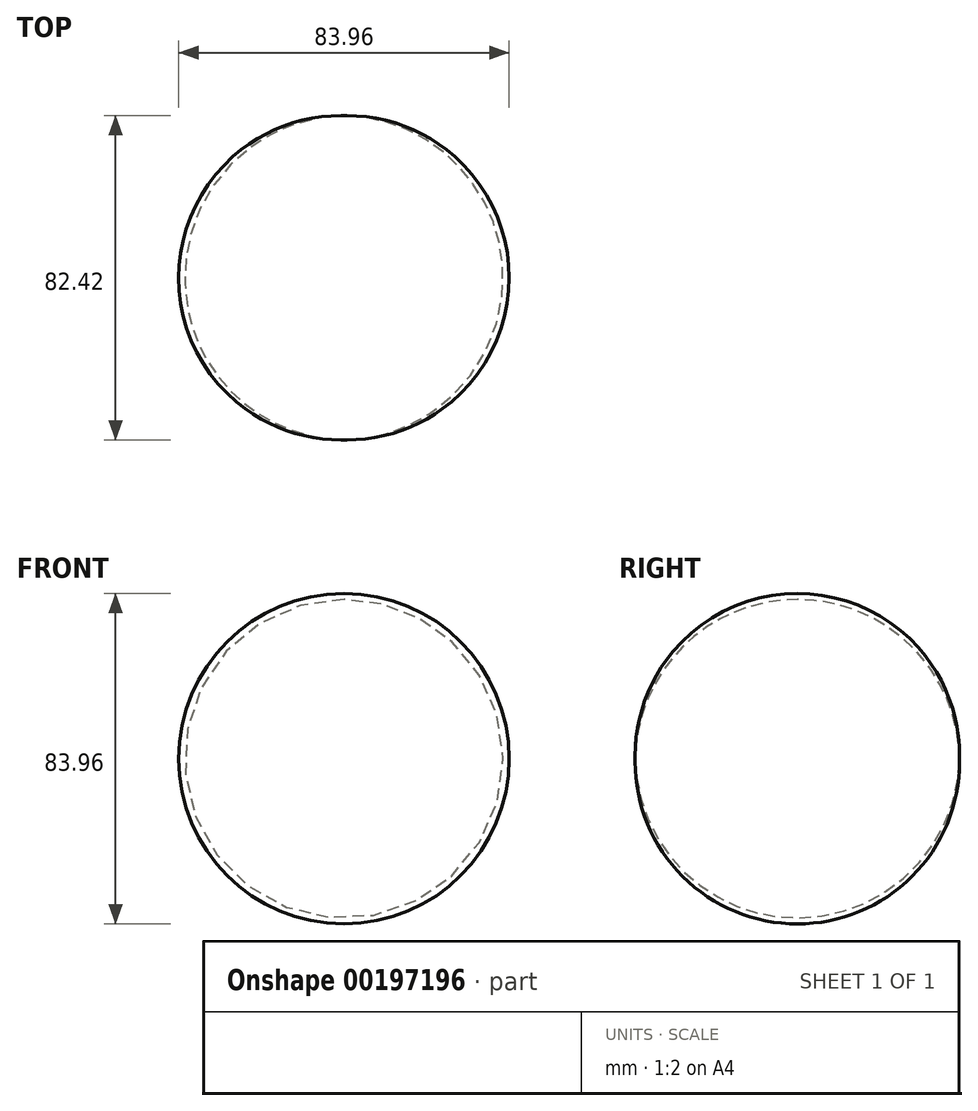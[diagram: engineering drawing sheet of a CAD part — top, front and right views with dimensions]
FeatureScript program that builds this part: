
annotation { "Feature Type Name" : "Feature", "Feature Type Description" : "" }
export const myFeature = defineFeature(function(context is Context, id is Id, definition is map)
    precondition{}
    {
        {
            var Q0;
            Q0=qCreatedBy(makeId("Right.planeOp"),FACE);
            var sketch = newSketch(context, id + "F0", { "sketchPlane" : qUnion([Q0])});
            skLineSegment(sketch, "E0", {"start": v(-60.6, 0) * mm, "end": v(62.45, 0) * mm});
            skArc(sketch, "E1", {"start": v(43.98, 0) * mm, "mid": v(2.77, 40.45) * mm, "end": v(-38.43, 0) * mm});
            skSolve(sketch);
        }
        {
            var Q0;
            Q0 = qSketchRegion(id + "F0", true);
            var Q1;
            Q1=sQuery(id+"F0.wireOp",EDGE,"E0");
            revolve(context, id + "F1", {"entities" : qUnion([Q0]), "axis" : qUnion([Q1]), "revolveType" : RevolveType.FULL});
        }
    });
